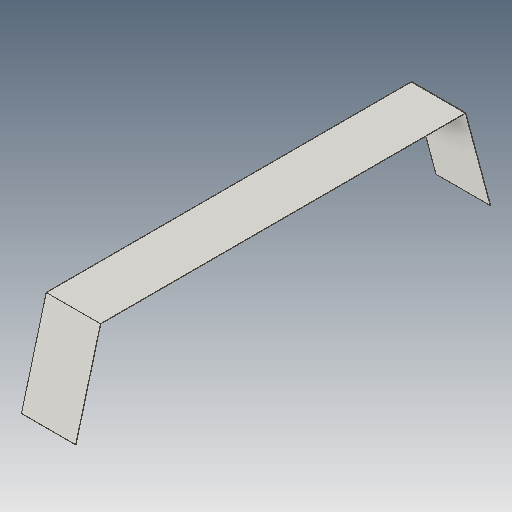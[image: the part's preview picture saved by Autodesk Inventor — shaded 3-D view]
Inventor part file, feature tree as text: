
AUTODESK INVENTOR PART (.ipt)
format: ipt  version: 2018 (Build 220112000, 112)  size: 87,040 bytes
history: native  units: in
note: dims shown in document units (in); Inventor stores cm internally (conversion verified against a paired STEP export)
features: other x3, sketch x1
ambient origin geometry x8: Origin, YZ Plane, XZ Plane, XY Plane, X Axis, Y Axis, Z Axis, Center Point
bodies: Solid1 (feature_tree)
feature tree (4):
  other  "Fender.ipt"
  other  "Solid1::Fender.ipt"
  other  "TaggingFeature1"
  sketch  "Sketch1"  dims[d0=0.3937in]
